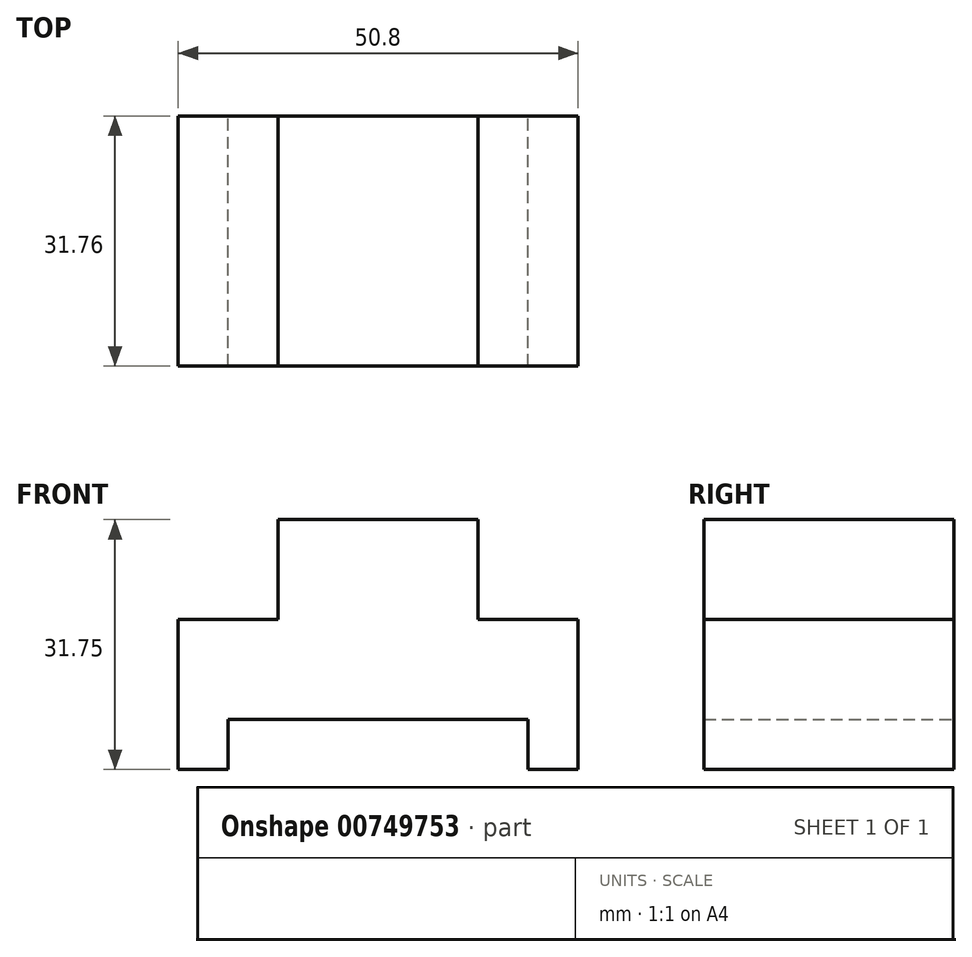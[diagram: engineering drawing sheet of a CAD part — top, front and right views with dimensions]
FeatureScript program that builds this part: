
annotation { "Feature Type Name" : "Feature", "Feature Type Description" : "" }
export const myFeature = defineFeature(function(context is Context, id is Id, definition is map)
    precondition{}
    {
        {
            var Q0;
            Q0=qCreatedBy(makeId("Front.planeOp"),FACE);
            var sketch = newSketch(context, id + "F0", { "sketchPlane" : qUnion([Q0])});
            skLineSegment(sketch, "E0", {"start": v(-19.67, -15.47) * mm, "end": v(-13.32, -15.47) * mm});
            skLineSegment(sketch, "E1", {"start": v(-13.32, -15.47) * mm, "end": v(-13.32, -9.12) * mm});
            skLineSegment(sketch, "E2", {"start": v(-13.32, -9.12) * mm, "end": v(24.78, -9.12) * mm});
            skLineSegment(sketch, "E3", {"start": v(24.78, -9.12) * mm, "end": v(24.78, -15.47) * mm});
            skLineSegment(sketch, "E4", {"start": v(24.78, -15.47) * mm, "end": v(31.13, -15.47) * mm});
            skLineSegment(sketch, "E5", {"start": v(31.13, -15.47) * mm, "end": v(31.13, 3.58) * mm});
            skLineSegment(sketch, "E6", {"start": v(31.13, 3.58) * mm, "end": v(18.43, 3.58) * mm});
            skLineSegment(sketch, "E7", {"start": v(18.43, 3.58) * mm, "end": v(18.43, 16.28) * mm});
            skLineSegment(sketch, "E8", {"start": v(18.43, 16.28) * mm, "end": v(-6.97, 16.28) * mm});
            skLineSegment(sketch, "E9", {"start": v(-6.97, 16.28) * mm, "end": v(-6.97, 3.58) * mm});
            skLineSegment(sketch, "E10", {"start": v(-6.97, 3.58) * mm, "end": v(-19.67, 3.58) * mm});
            skLineSegment(sketch, "E11", {"start": v(-19.67, 3.58) * mm, "end": v(-19.67, -15.47) * mm});
            skSolve(sketch);
        }
        {
            var Q0;
            Q0 = qSketchRegion(id + "F0", true);
            extrude(context, id + "F1", {"entities" : qUnion([Q0]), "endBound" : BoundingType.SYMMETRIC, "depth" : 31.75 * mm, "offsetDistance" : 25.4 * mm});
        }
    });
